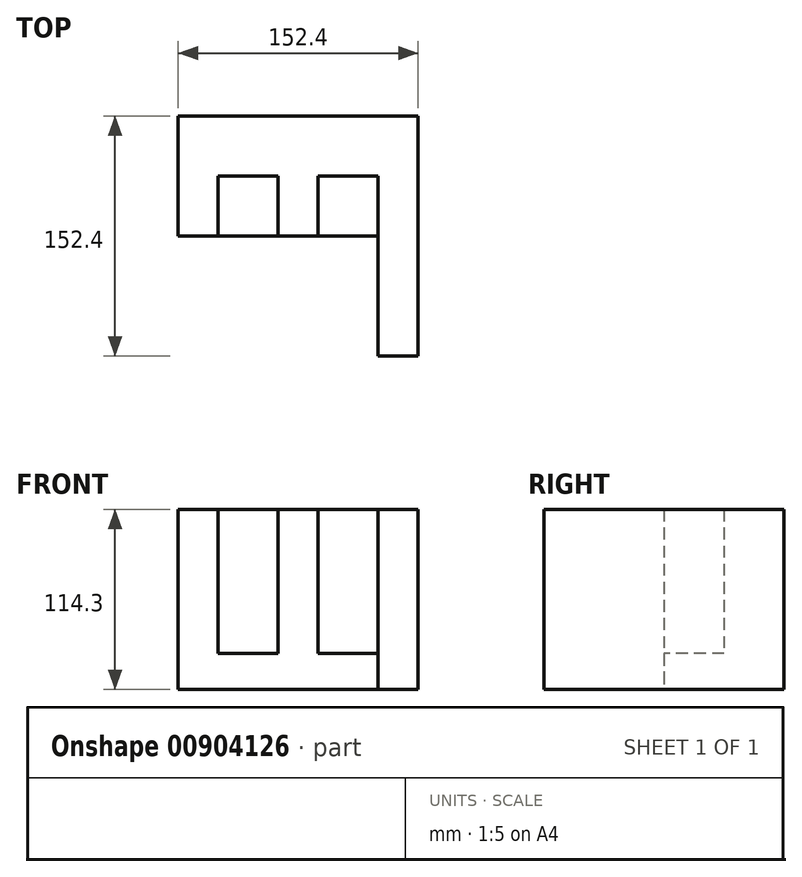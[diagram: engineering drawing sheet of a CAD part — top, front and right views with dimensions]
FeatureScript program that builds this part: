
annotation { "Feature Type Name" : "Feature", "Feature Type Description" : "" }
export const myFeature = defineFeature(function(context is Context, id is Id, definition is map)
    precondition{}
    {
        {
            var Q0;
            Q0=qCreatedBy(makeId("Front.planeOp"),FACE);
            var sketch = newSketch(context, id + "F0", { "sketchPlane" : qUnion([Q0])});
            skLineSegment(sketch, "E0.bottom", {"start": v(-76.2, 57.15) * mm, "end": v(76.2, 57.15) * mm});
            skLineSegment(sketch, "E0.top", {"start": v(-76.2, -57.15) * mm, "end": v(76.2, -57.15) * mm});
            skLineSegment(sketch, "E0.left", {"start": v(-76.2, 57.15) * mm, "end": v(-76.2, -57.15) * mm});
            skLineSegment(sketch, "E0.right", {"start": v(76.2, 57.15) * mm, "end": v(76.2, -57.15) * mm});
            skPoint(sketch, "E0.middle", {"position": v(0, 0) * mm});
            skSolve(sketch);
        }
        {
            var Q0;
            Q0=makeQuery(id+"F0.imprint","IMPRINT",FACE,{"disambiguationData":[TD([[makeQuery(id+"F0.imprint","IMPRINT",EDGE,{"derivedFrom":sQuery(id+"F0.wireOp",EDGE,"E0.bottom")}),-1.0]])]});
            extrude(context, id + "F1", {"entities" : qUnion([Q0]), "depth" : 152.4 * mm, "offsetDistance" : 25.4 * mm});
        }
        {
            var Q0;
            Q0=makeQuery(id+"F1.opExtrude","CAP_FACE",FACE,{"disambiguationData":[OSD([sQuery(id+"F0.wireOp",EDGE,"E0.bottom"),sQuery(id+"F0.wireOp",EDGE,"E0.top"),sQuery(id+"F0.wireOp",EDGE,"E0.left"),sQuery(id+"F0.wireOp",EDGE,"E0.right")])],"isStart":false});
            var sketch = newSketch(context, id + "F2", { "sketchPlane" : qUnion([Q0])});
            skLineSegment(sketch, "E1", {"start": v(50.8, 57.15) * mm, "end": v(50.8, -57.15) * mm});
            skSolve(sketch);
        }
        {
            var Q0;
            {var subQ0=sQuery(id+"F2.wireOp",EDGE,"E1");Q0=makeQuery(id+"F2.imprint","IMPRINT",FACE,{"disambiguationData":[TD([[makeQuery(id+"F2.imprint","IMPRINT",EDGE,{"derivedFrom":subQ0}),-1.0]])]});}
            extrude(context, id + "F3", {"entities" : qUnion([Q0]), "operationType" : NewBodyOperationType.REMOVE, "oppositeDirection" : true, "depth" : 76.2 * mm, "offsetDistance" : 25.4 * mm});
        }
        {
            var Q0;
            Q0=makeQuery(id+"F3.boolean.opBoolean","COPY",FACE,{"derivedFrom":makeQuery(id+"F3.opExtrude","CAP_FACE",FACE,{"disambiguationData":[OSD([sQuery(id+"F0.wireOp",EDGE,"E0.bottom"),sQuery(id+"F0.wireOp",EDGE,"E0.top"),sQuery(id+"F0.wireOp",EDGE,"E0.left"),sQuery(id+"F2.wireOp",EDGE,"E1")])],"isStart":false})});
            var sketch = newSketch(context, id + "F4", { "sketchPlane" : qUnion([Q0])});
            skLineSegment(sketch, "E2.bottom", {"start": v(-50.8, 57.15) * mm, "end": v(-12.7, 57.15) * mm});
            skLineSegment(sketch, "E2.top", {"start": v(-50.8, -34.3) * mm, "end": v(-12.7, -34.3) * mm});
            skLineSegment(sketch, "E2.left", {"start": v(-50.8, 57.15) * mm, "end": v(-50.8, -34.3) * mm});
            skLineSegment(sketch, "E2.right", {"start": v(-12.7, 57.15) * mm, "end": v(-12.7, -34.29) * mm});
            skLineSegment(sketch, "E3.bottom", {"start": v(50.8, 57.15) * mm, "end": v(12.7, 57.15) * mm});
            skLineSegment(sketch, "E3.top", {"start": v(50.8, -34.3) * mm, "end": v(12.7, -34.3) * mm});
            skLineSegment(sketch, "E3.left", {"start": v(50.8, 57.15) * mm, "end": v(50.8, -34.3) * mm});
            skLineSegment(sketch, "E3.right", {"start": v(12.7, 57.15) * mm, "end": v(12.7, -34.3) * mm});
            skSolve(sketch);
        }
        {
            var Q0;
            Q0=makeQuery(id+"F4.imprint","IMPRINT",FACE,{"disambiguationData":[TD([[makeQuery(id+"F4.imprint","IMPRINT",EDGE,{"derivedFrom":sQuery(id+"F4.wireOp",EDGE,"E2.bottom")}),-1.0]])]});
            extrude(context, id + "F5", {"entities" : qUnion([Q0]), "operationType" : NewBodyOperationType.REMOVE, "oppositeDirection" : true, "depth" : 38.1 * mm, "offsetDistance" : 25.4 * mm});
        }
        {
            var Q0;
            Q0=makeQuery(id+"F4.imprint","IMPRINT",FACE,{"disambiguationData":[TD([[makeQuery(id+"F4.imprint","IMPRINT",EDGE,{"derivedFrom":sQuery(id+"F4.wireOp",EDGE,"E3.bottom")}),-1.0]])]});
            extrude(context, id + "F6", {"entities" : qUnion([Q0]), "operationType" : NewBodyOperationType.REMOVE, "oppositeDirection" : true, "depth" : 38.1 * mm, "offsetDistance" : 25.4 * mm});
        }
    });
